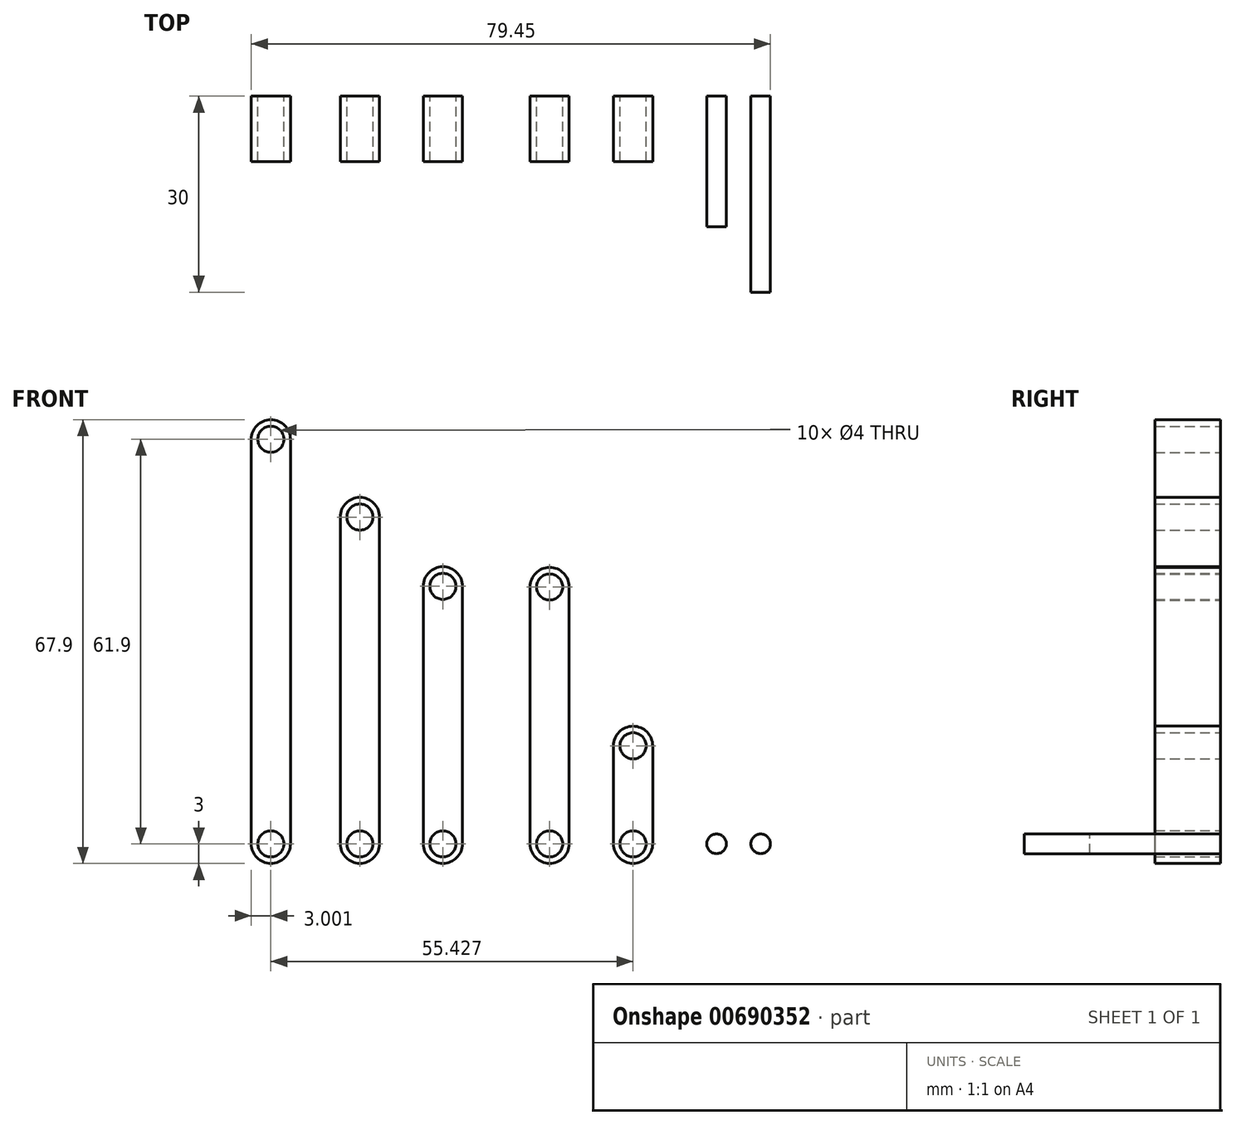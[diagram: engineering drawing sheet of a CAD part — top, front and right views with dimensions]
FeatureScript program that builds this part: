
annotation { "Feature Type Name" : "Feature", "Feature Type Description" : "" }
export const myFeature = defineFeature(function(context is Context, id is Id, definition is map)
    precondition{}
    {
        {
            assignVariable(context, id + "F0", {"name" : "thinkness", "anyValue" : 10});
        }
        {
            var Q0;
            Q0=qCreatedBy(makeId("Front.planeOp"),FACE);
            var sketch = newSketch(context, id + "F1", { "sketchPlane" : qUnion([Q0])});
            skArc(sketch, "E0", {"start": v(-15.77, 0) * mm, "mid": v(-12.77, -3) * mm, "end": v(-9.77, 0) * mm});
            skArc(sketch, "E1", {"start": v(-9.77, 15) * mm, "mid": v(-12.77, 18) * mm, "end": v(-15.77, 15) * mm});
            skLineSegment(sketch, "E2", {"start": v(-15.77, 15) * mm, "end": v(-15.77, 0) * mm});
            skLineSegment(sketch, "E3", {"start": v(-9.77, 0) * mm, "end": v(-9.77, 15) * mm});
            skCircle(sketch, "E4", {"center": v(-12.77, 15) * mm, "radius": 2 * mm});
            skCircle(sketch, "E5", {"center": v(-12.77, 0) * mm, "radius": 2 * mm});
            skSolve(sketch);
        }
        {
            var Q0;
            Q0=makeQuery(id+"F1.imprint","IMPRINT",FACE,{"disambiguationData":[TD([[makeQuery(id+"F1.imprint","IMPRINT",EDGE,{"derivedFrom":sQuery(id+"F1.wireOp",EDGE,"E0")}),1.0]])]});
            extrude(context, id + "F2", {"entities" : qUnion([Q0]), "depth" : (getVariable(context, 'thinkness')) * mm, "offsetDistance" : 25 * mm});
        }
        {
            var Q0;
            Q0=qCreatedBy(makeId("Front.planeOp"),FACE);
            var sketch = newSketch(context, id + "F3", { "sketchPlane" : qUnion([Q0])});
            skArc(sketch, "E6", {"start": v(-28.54, 0) * mm, "mid": v(-25.54, -3) * mm, "end": v(-22.54, 0) * mm});
            skArc(sketch, "E7", {"start": v(-22.54, 39.3) * mm, "mid": v(-25.54, 42.3) * mm, "end": v(-28.54, 39.3) * mm});
            skLineSegment(sketch, "E8", {"start": v(-28.54, 39.3) * mm, "end": v(-28.54, 0) * mm});
            skLineSegment(sketch, "E9", {"start": v(-22.54, 0) * mm, "end": v(-22.54, 39.3) * mm});
            skCircle(sketch, "E10", {"center": v(-25.54, 39.3) * mm, "radius": 2 * mm});
            skCircle(sketch, "E11", {"center": v(-25.54, 0) * mm, "radius": 2 * mm});
            skSolve(sketch);
        }
        {
            var Q0;
            Q0=makeQuery(id+"F3.imprint","IMPRINT",FACE,{"disambiguationData":[TD([[makeQuery(id+"F3.imprint","IMPRINT",EDGE,{"derivedFrom":sQuery(id+"F3.wireOp",EDGE,"E6")}),1.0]])]});
            extrude(context, id + "F4", {"entities" : qUnion([Q0]), "depth" : (getVariable(context, 'thinkness')) * mm, "offsetDistance" : 25 * mm});
        }
        {
            var Q0;
            Q0=qCreatedBy(makeId("Front.planeOp"),FACE);
            var sketch = newSketch(context, id + "F5", { "sketchPlane" : qUnion([Q0])});
            skArc(sketch, "E12", {"start": v(-44.88, 0) * mm, "mid": v(-41.88, -3) * mm, "end": v(-38.88, 0) * mm});
            skArc(sketch, "E13", {"start": v(-38.88, 39.4) * mm, "mid": v(-41.88, 42.4) * mm, "end": v(-44.88, 39.4) * mm});
            skLineSegment(sketch, "E14", {"start": v(-44.88, 39.4) * mm, "end": v(-44.88, 0) * mm});
            skLineSegment(sketch, "E15", {"start": v(-38.88, 0) * mm, "end": v(-38.88, 39.4) * mm});
            skCircle(sketch, "E16", {"center": v(-41.88, 39.4) * mm, "radius": 2 * mm});
            skCircle(sketch, "E17", {"center": v(-41.88, 0) * mm, "radius": 2 * mm});
            skSolve(sketch);
        }
        {
            var Q0;
            Q0=makeQuery(id+"F5.imprint","IMPRINT",FACE,{"disambiguationData":[TD([[makeQuery(id+"F5.imprint","IMPRINT",EDGE,{"derivedFrom":sQuery(id+"F5.wireOp",EDGE,"E12")}),1.0]])]});
            extrude(context, id + "F6", {"entities" : qUnion([Q0]), "depth" : (getVariable(context, 'thinkness')) * mm, "offsetDistance" : 25 * mm});
        }
        {
            var Q0;
            Q0=qCreatedBy(makeId("Front.planeOp"),FACE);
            var sketch = newSketch(context, id + "F7", { "sketchPlane" : qUnion([Q0])});
            skArc(sketch, "E18", {"start": v(-57.57, 0) * mm, "mid": v(-54.57, -3) * mm, "end": v(-51.57, 0) * mm});
            skArc(sketch, "E19", {"start": v(-51.57, 50) * mm, "mid": v(-54.57, 53) * mm, "end": v(-57.57, 50) * mm});
            skLineSegment(sketch, "E20", {"start": v(-57.57, 50) * mm, "end": v(-57.57, 0) * mm});
            skLineSegment(sketch, "E21", {"start": v(-51.57, 0) * mm, "end": v(-51.57, 50) * mm});
            skCircle(sketch, "E22", {"center": v(-54.57, 50) * mm, "radius": 2 * mm});
            skCircle(sketch, "E23", {"center": v(-54.57, 0) * mm, "radius": 2 * mm});
            skSolve(sketch);
        }
        {
            var Q0;
            Q0=makeQuery(id+"F7.imprint","IMPRINT",FACE,{"disambiguationData":[TD([[makeQuery(id+"F7.imprint","IMPRINT",EDGE,{"derivedFrom":sQuery(id+"F7.wireOp",EDGE,"E18")}),1.0]])]});
            extrude(context, id + "F8", {"entities" : qUnion([Q0]), "depth" : (getVariable(context, 'thinkness')) * mm, "offsetDistance" : 25 * mm});
        }
        {
            var Q0;
            Q0=qCreatedBy(makeId("Front.planeOp"),FACE);
            var sketch = newSketch(context, id + "F9", { "sketchPlane" : qUnion([Q0])});
            skArc(sketch, "E24", {"start": v(-71.2, 0) * mm, "mid": v(-68.2, -3) * mm, "end": v(-65.2, 0) * mm});
            skArc(sketch, "E25", {"start": v(-65.2, 61.9) * mm, "mid": v(-68.2, 64.9) * mm, "end": v(-71.2, 61.9) * mm});
            skLineSegment(sketch, "E26", {"start": v(-71.2, 61.9) * mm, "end": v(-71.2, 0) * mm});
            skLineSegment(sketch, "E27", {"start": v(-65.2, 0) * mm, "end": v(-65.2, 61.9) * mm});
            skCircle(sketch, "E28", {"center": v(-68.2, 61.9) * mm, "radius": 2 * mm});
            skCircle(sketch, "E29", {"center": v(-68.2, 0) * mm, "radius": 2 * mm});
            skSolve(sketch);
        }
        {
            var Q0;
            Q0=makeQuery(id+"F9.imprint","IMPRINT",FACE,{"disambiguationData":[TD([[makeQuery(id+"F9.imprint","IMPRINT",EDGE,{"derivedFrom":sQuery(id+"F9.wireOp",EDGE,"E24")}),1.0]])]});
            extrude(context, id + "F10", {"entities" : qUnion([Q0]), "depth" : (getVariable(context, 'thinkness')) * mm, "offsetDistance" : 25 * mm});
        }
        {
            var Q0;
            Q0=qCreatedBy(makeId("Front.planeOp"),FACE);
            var sketch = newSketch(context, id + "F11", { "sketchPlane" : qUnion([Q0])});
            skCircle(sketch, "E30", {"center": v(0, 0) * mm, "radius": 1.5 * mm});
            skSolve(sketch);
        }
        {
            var Q0;
            Q0 = qSketchRegion(id + "F11", true);
            extrude(context, id + "F12", {"entities" : qUnion([Q0]), "depth" : (getVariable(context, 'thinkness') * 2) * mm, "offsetDistance" : 25 * mm});
        }
        {
            var Q0;
            Q0=qCreatedBy(makeId("Front.planeOp"),FACE);
            var sketch = newSketch(context, id + "F13", { "sketchPlane" : qUnion([Q0])});
            skCircle(sketch, "E31", {"center": v(6.75, 0) * mm, "radius": 1.5 * mm});
            skSolve(sketch);
        }
        {
            var Q0;
            Q0=makeQuery(id+"F13.imprint","IMPRINT",FACE,{"disambiguationData":[TD([[makeQuery(id+"F13.imprint","IMPRINT",EDGE,{"derivedFrom":sQuery(id+"F13.wireOp",EDGE,"E31")}),1.0]])]});
            extrude(context, id + "F14", {"entities" : qUnion([Q0]), "depth" : (getVariable(context, 'thinkness') * 3) * mm, "offsetDistance" : 25 * mm});
        }
    });
